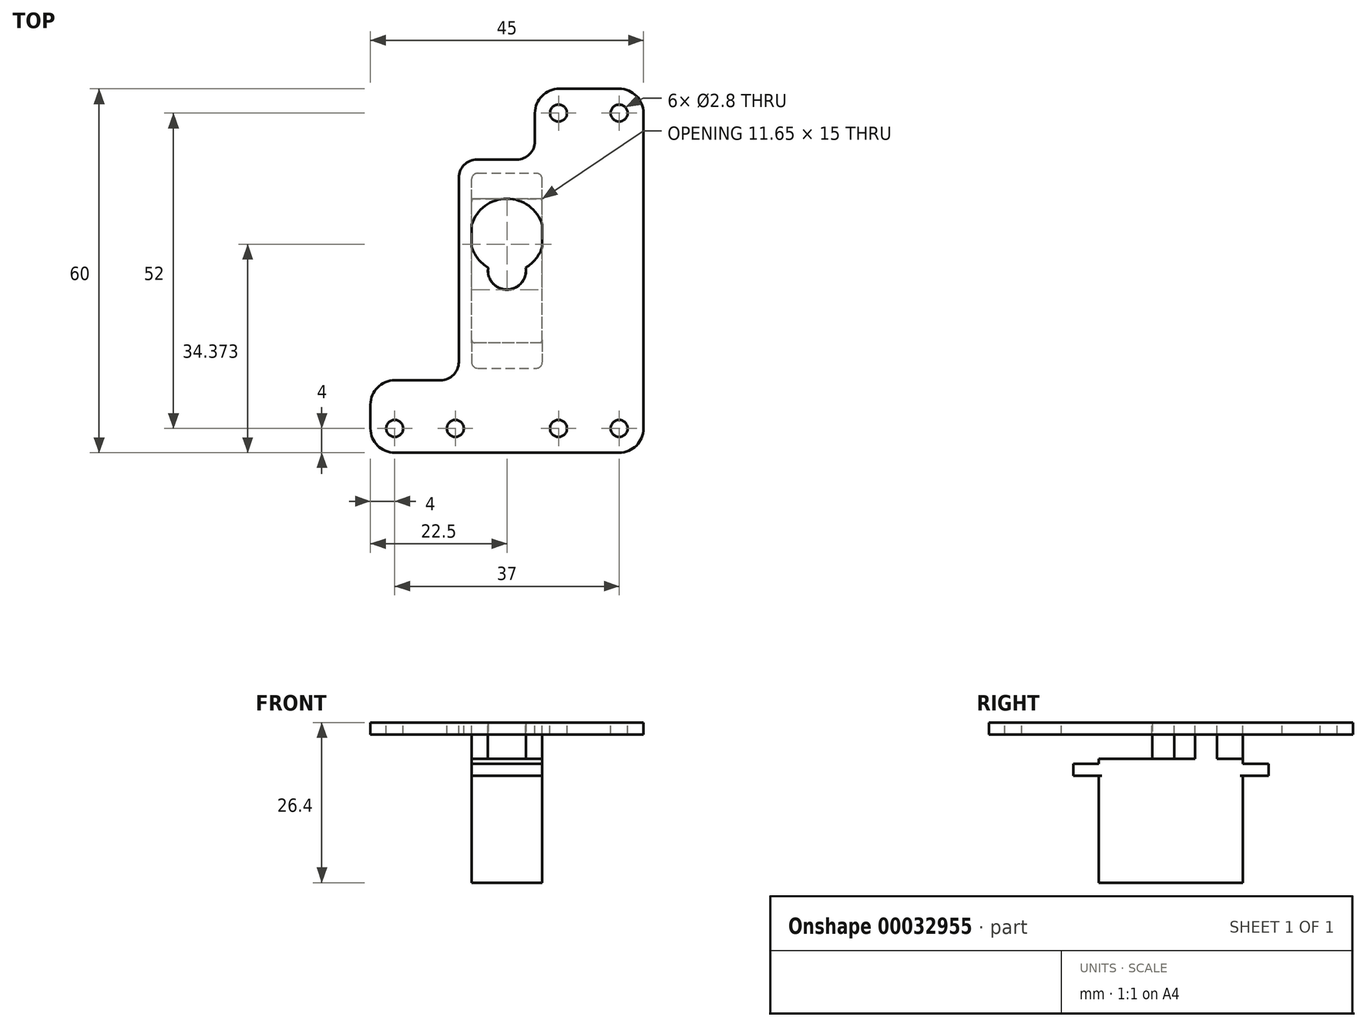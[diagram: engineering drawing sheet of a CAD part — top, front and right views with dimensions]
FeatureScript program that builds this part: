
annotation { "Feature Type Name" : "Feature", "Feature Type Description" : "" }
export const myFeature = defineFeature(function(context is Context, id is Id, definition is map)
    precondition{}
    {
        {
            var Q0;
            Q0=qCreatedBy(makeId("Top.planeOp"),FACE);
            var sketch = newSketch(context, id + "F0", { "sketchPlane" : qUnion([Q0])});
            skLineSegment(sketch, "E0.rect.bottom", {"start": v(5.82, -11.88) * mm, "end": v(-5.83, -11.88) * mm});
            skLineSegment(sketch, "E0.rect.top", {"start": v(5.83, 11.88) * mm, "end": v(-5.82, 11.88) * mm});
            skLineSegment(sketch, "E0.rect.left", {"start": v(5.82, -11.88) * mm, "end": v(5.83, 11.88) * mm});
            skLineSegment(sketch, "E0.rect.right", {"start": v(-5.83, -11.88) * mm, "end": v(-5.82, 11.87) * mm});
            skPoint(sketch, "E0.rect.middle", {"position": v(0, 0) * mm});
            skSolve(sketch);
        }
        {
            var Q0;
            Q0 = qSketchRegion(id + "F0", true);
            extrude(context, id + "F1", {"entities" : qUnion([Q0]), "depth" : 20.4 * mm});
        }
        {
            var Q0;
            Q0=makeQuery(id+"F1.opExtrude","CAP_FACE",FACE,{"disambiguationData":[OSD([sQuery(id+"F0.wireOp",EDGE,"E0.rect.bottom"),sQuery(id+"F0.wireOp",EDGE,"E0.rect.top"),sQuery(id+"F0.wireOp",EDGE,"E0.rect.left"),sQuery(id+"F0.wireOp",EDGE,"E0.rect.right")])],"isStart":false});
            var sketch = newSketch(context, id + "F2", { "sketchPlane" : qUnion([Q0])});
            skArc(sketch, "E1", {"start": v(5.83, 7.59) * mm, "mid": v(0, 11.88) * mm, "end": v(-5.83, 7.59) * mm});
            skLineSegment(sketch, "E2", {"start": v(5.83, 7.59) * mm, "end": v(5.83, 3.96) * mm});
            skLineSegment(sketch, "E3.MirrorCS", {"start": v(-5.83, 7.59) * mm, "end": v(-5.83, 3.96) * mm});
            skArc(sketch, "E4.trimOffspring", {"start": v(-5.83, 3.96) * mm, "mid": v(-4.78, 1.98) * mm, "end": v(-3.09, 0.51) * mm});
            skArc(sketch, "E5", {"start": v(-3.09, 0.51) * mm, "mid": v(0, -3.1) * mm, "end": v(3.09, 0.51) * mm});
            skArc(sketch, "E6.trimOffspring", {"start": v(3.09, 0.51) * mm, "mid": v(4.78, 1.98) * mm, "end": v(5.83, 3.96) * mm});
            skSolve(sketch);
        }
        {
            var Q0;
            Q0 = qSketchRegion(id + "F2", true);
            extrude(context, id + "F3", {"entities" : qUnion([Q0]), "operationType" : NewBodyOperationType.ADD, "depth" : 6 * mm});
        }
        {
            var Q0;
            {var subQ0=sQuery(id+"F0.wireOp",EDGE,"E0.rect.bottom");var subQ1=sQuery(id+"F0.wireOp",EDGE,"E0.rect.left");var subQ2=sQuery(id+"F0.wireOp",EDGE,"E0.rect.right");Q0=makeQuery(id+"F3.boolean.opBoolean","SPLIT",FACE,{"disambiguationData":[TD([makeQuery(id+"F1.opExtrude","SWEPT_FACE",FACE,{"disambiguationData":[OSD([subQ0])]}),makeQuery(id+"F1.opExtrude","SWEPT_FACE",FACE,{"disambiguationData":[OSD([subQ1])]}),makeQuery(id+"F1.opExtrude","SWEPT_FACE",FACE,{"disambiguationData":[OSD([subQ2])]}),makeQuery(id+"F3.opExtrude","SWEPT_FACE",FACE,{"disambiguationData":[OSD([sQuery(id+"F2.wireOp",EDGE,"E2")])]}),makeQuery(id+"F3.opExtrude","SWEPT_FACE",FACE,{"disambiguationData":[OSD([sQuery(id+"F2.wireOp",EDGE,"E3.MirrorCS")])]}),makeQuery(id+"F3.opExtrude","SWEPT_FACE",FACE,{"disambiguationData":[OSD([sQuery(id+"F2.wireOp",EDGE,"E4.trimOffspring")])]}),makeQuery(id+"F3.opExtrude","SWEPT_FACE",FACE,{"disambiguationData":[OSD([sQuery(id+"F2.wireOp",EDGE,"E5")])]}),makeQuery(id+"F3.opExtrude","SWEPT_FACE",FACE,{"disambiguationData":[OSD([sQuery(id+"F2.wireOp",EDGE,"E6.trimOffspring")])]})])],"derivedFrom":makeQuery(id+"F1.opExtrude","CAP_FACE",FACE,{"disambiguationData":[OSD([subQ0,sQuery(id+"F0.wireOp",EDGE,"E0.rect.top"),subQ1,subQ2])],"isStart":false})});}
            var sketch = newSketch(context, id + "F4", { "sketchPlane" : qUnion([Q0])});
            skLineSegment(sketch, "E7.bottom", {"start": v(-5.83, -11.88) * mm, "end": v(5.82, -11.88) * mm});
            skLineSegment(sketch, "E7.top", {"start": v(-5.83, -16.08) * mm, "end": v(5.82, -16.08) * mm});
            skLineSegment(sketch, "E7.left", {"start": v(-5.83, -11.88) * mm, "end": v(-5.83, -16.08) * mm});
            skLineSegment(sketch, "E7.right", {"start": v(5.82, -11.88) * mm, "end": v(5.82, -16.08) * mm});
            skLineSegment(sketch, "E8.MirrorCS", {"start": v(-5.83, 11.88) * mm, "end": v(-5.83, 16.08) * mm});
            skLineSegment(sketch, "E9.MirrorCS", {"start": v(-5.83, 16.08) * mm, "end": v(5.82, 16.08) * mm});
            skLineSegment(sketch, "E10.MirrorCS", {"start": v(5.82, 11.88) * mm, "end": v(5.82, 16.08) * mm});
            skLineSegment(sketch, "E11.MirrorCS", {"start": v(-5.83, 11.88) * mm, "end": v(5.82, 11.88) * mm});
            skSolve(sketch);
        }
        {
            var Q0;
            Q0=makeQuery(id+"F4.imprint","IMPRINT",FACE,{"disambiguationData":[TD([[makeQuery(id+"F4.imprint","IMPRINT",EDGE,{"derivedFrom":sQuery(id+"F4.wireOp",EDGE,"E7.bottom")}),1.0]])]});
            var Q1;
            Q1=makeQuery(id+"F4.imprint","IMPRINT",FACE,{"disambiguationData":[TD([[makeQuery(id+"F4.imprint","IMPRINT",EDGE,{"derivedFrom":sQuery(id+"F4.wireOp",EDGE,"E8.MirrorCS")}),-1.0]])]});
            extrude(context, id + "F5", {"entities" : qUnion([Q0, Q1]), "operationType" : NewBodyOperationType.ADD, "oppositeDirection" : true, "depth" : 2.8 * mm, "hasSecondDirection" : true, "secondDirectionOppositeDirection" : true, "secondDirectionDepth" : .8 * mm});
        }
        {
            var Q0;
            {var subQ0=sQuery(id+"F0.wireOp",EDGE,"E0.rect.top");var subQ1=sQuery(id+"F0.wireOp",EDGE,"E0.rect.left");Q0=makeQuery(id+"F5.boolean.opBoolean","SPLIT",EDGE,{"disambiguationData":[TD([makeQuery(id+"F1.opExtrude","CAP_FACE",FACE,{"disambiguationData":[OSD([sQuery(id+"F0.wireOp",EDGE,"E0.rect.bottom"),subQ0,subQ1,sQuery(id+"F0.wireOp",EDGE,"E0.rect.right")])],"isStart":true})])],"derivedFrom":makeQuery(id+"F1.opExtrude","SWEPT_EDGE",EDGE,{"disambiguationData":[OSD([subQ0,subQ1])]})});}
            var Q1;
            {var subQ0=sQuery(id+"F0.wireOp",EDGE,"E0.rect.bottom");var subQ1=sQuery(id+"F0.wireOp",EDGE,"E0.rect.left");Q1=makeQuery(id+"F5.boolean.opBoolean","SPLIT",EDGE,{"disambiguationData":[TD([makeQuery(id+"F1.opExtrude","CAP_FACE",FACE,{"disambiguationData":[OSD([subQ0,sQuery(id+"F0.wireOp",EDGE,"E0.rect.top"),subQ1,sQuery(id+"F0.wireOp",EDGE,"E0.rect.right")])],"isStart":true})])],"derivedFrom":makeQuery(id+"F1.opExtrude","SWEPT_EDGE",EDGE,{"disambiguationData":[OSD([subQ0,subQ1])]})});}
            var Q2;
            {var subQ0=sQuery(id+"F0.wireOp",EDGE,"E0.rect.bottom");var subQ1=sQuery(id+"F0.wireOp",EDGE,"E0.rect.right");Q2=makeQuery(id+"F5.boolean.opBoolean","SPLIT",EDGE,{"disambiguationData":[TD([makeQuery(id+"F1.opExtrude","CAP_FACE",FACE,{"disambiguationData":[OSD([subQ0,sQuery(id+"F0.wireOp",EDGE,"E0.rect.top"),sQuery(id+"F0.wireOp",EDGE,"E0.rect.left"),subQ1])],"isStart":true})])],"derivedFrom":makeQuery(id+"F1.opExtrude","SWEPT_EDGE",EDGE,{"disambiguationData":[OSD([subQ0,subQ1])]})});}
            var Q3;
            {var subQ0=sQuery(id+"F0.wireOp",EDGE,"E0.rect.top");var subQ1=sQuery(id+"F0.wireOp",EDGE,"E0.rect.right");Q3=makeQuery(id+"F5.boolean.opBoolean","SPLIT",EDGE,{"disambiguationData":[TD([makeQuery(id+"F1.opExtrude","CAP_FACE",FACE,{"disambiguationData":[OSD([sQuery(id+"F0.wireOp",EDGE,"E0.rect.bottom"),subQ0,sQuery(id+"F0.wireOp",EDGE,"E0.rect.left"),subQ1])],"isStart":true})])],"derivedFrom":makeQuery(id+"F1.opExtrude","SWEPT_EDGE",EDGE,{"disambiguationData":[OSD([subQ0,subQ1])]})});}
            fillet(context, id + "F6", {"entities" : qUnion([Q0, Q1, Q2, Q3]), "radius" : .5 * mm, "tangentPropagation" : true, "allowEdgeOverflow" : false});
        }
        {
            var Q0;
            Q0=makeQuery(id+"F5.opExtrude","SWEPT_EDGE",EDGE,{"disambiguationData":[OSD([sQuery(id+"F4.wireOp",EDGE,"E8.MirrorCS"),sQuery(id+"F4.wireOp",EDGE,"E9.MirrorCS")])]});
            var Q1;
            Q1=makeQuery(id+"F5.opExtrude","SWEPT_EDGE",EDGE,{"disambiguationData":[OSD([sQuery(id+"F4.wireOp",EDGE,"E9.MirrorCS"),sQuery(id+"F4.wireOp",EDGE,"E10.MirrorCS")])]});
            var Q2;
            Q2=makeQuery(id+"F5.opExtrude","SWEPT_EDGE",EDGE,{"disambiguationData":[OSD([sQuery(id+"F4.wireOp",EDGE,"E7.top"),sQuery(id+"F4.wireOp",EDGE,"E7.right")])]});
            var Q3;
            Q3=makeQuery(id+"F5.opExtrude","SWEPT_EDGE",EDGE,{"disambiguationData":[OSD([sQuery(id+"F4.wireOp",EDGE,"E7.top"),sQuery(id+"F4.wireOp",EDGE,"E7.left")])]});
            fillet(context, id + "F7", {"entities" : qUnion([Q0, Q1, Q2, Q3]), "radius" : 1 * mm, "tangentPropagation" : true, "allowEdgeOverflow" : false});
        }
        {
            var Q0;
            Q0=makeQuery(id+"F3.opExtrude","CAP_FACE",FACE,{"disambiguationData":[OSD([sQuery(id+"F2.wireOp",EDGE,"E1"),sQuery(id+"F2.wireOp",EDGE,"E2"),sQuery(id+"F2.wireOp",EDGE,"E3.MirrorCS"),sQuery(id+"F2.wireOp",EDGE,"E4.trimOffspring"),sQuery(id+"F2.wireOp",EDGE,"E5"),sQuery(id+"F2.wireOp",EDGE,"E6.trimOffspring")])],"isStart":false});
            var sketch = newSketch(context, id + "F8", { "sketchPlane" : qUnion([Q0])});
            skArc(sketch, "E12", {"start": v(3.09, 0.51) * mm, "mid": v(4.78, 1.98) * mm, "end": v(5.83, 3.96) * mm});
            skArc(sketch, "E13", {"start": v(-3.09, 0.51) * mm, "mid": v(0, -3.13) * mm, "end": v(3.09, 0.51) * mm});
            skLineSegment(sketch, "E14", {"start": v(-5.83, 3.96) * mm, "end": v(-5.83, 7.59) * mm});
            skLineSegment(sketch, "E15.MirrorCS", {"start": v(5.83, 3.96) * mm, "end": v(5.83, 7.59) * mm});
            skArc(sketch, "E16.trimOffspring", {"start": v(-5.83, 3.96) * mm, "mid": v(-4.78, 1.98) * mm, "end": v(-3.09, 0.51) * mm});
            skArc(sketch, "E17.trimOffspring", {"start": v(5.83, 7.59) * mm, "mid": v(0, 11.88) * mm, "end": v(-5.83, 7.59) * mm});
            skLineSegment(sketch, "E18.rect.bottom", {"start": v(22.5, 30) * mm, "end": v(4.61, 30) * mm});
            skLineSegment(sketch, "E18.rect.top", {"start": v(22.5, -30) * mm, "end": v(-22.5, -30) * mm});
            skLineSegment(sketch, "E18.rect.left", {"start": v(22.5, 30) * mm, "end": v(22.5, -30) * mm});
            skLineSegment(sketch, "E18.rect.right", {"start": v(-22.5, -18.07) * mm, "end": v(-22.5, -30) * mm});
            skLineSegment(sketch, "E19.bottom", {"start": v(-22.5, -30) * mm, "end": v(-18.5, -30) * mm, "construction": true});
            skLineSegment(sketch, "E19.top", {"start": v(-22.5, -26) * mm, "end": v(-18.5, -26) * mm, "construction": true});
            skLineSegment(sketch, "E19.left", {"start": v(-22.5, -30) * mm, "end": v(-22.5, -26) * mm, "construction": true});
            skLineSegment(sketch, "E19.right", {"start": v(-18.5, -30) * mm, "end": v(-18.5, -26) * mm, "construction": true});
            skCircle(sketch, "E20", {"center": v(-18.5, -26) * mm, "radius": 1.4 * mm});
            skCircle(sketch, "E21.MirrorC", {"center": v(18.5, -26) * mm, "radius": 1.4 * mm});
            skCircle(sketch, "E22.MirrorC", {"center": v(18.5, 26) * mm, "radius": 1.4 * mm});
            skCircle(sketch, "E23", {"center": v(-8.5, -26) * mm, "radius": 1.4 * mm});
            skCircle(sketch, "E24.MirrorC", {"center": v(8.5, -26) * mm, "radius": 1.4 * mm});
            skCircle(sketch, "E25.MirrorC", {"center": v(8.5, 26) * mm, "radius": 1.4 * mm});
            skLineSegment(sketch, "E26", {"start": v(4.61, 30) * mm, "end": v(4.61, 21.32) * mm});
            skLineSegment(sketch, "E27", {"start": v(1.61, 18.32) * mm, "end": v(-4.94, 18.32) * mm});
            skLineSegment(sketch, "E28", {"start": v(-7.94, 15.32) * mm, "end": v(-7.94, -15.07) * mm});
            skLineSegment(sketch, "E29", {"start": v(-10.94, -18.07) * mm, "end": v(-22.5, -18.07) * mm});
            skPoint(sketch, "E30.orphan", {"position": v(-22.5, 30) * mm});
            skPoint(sketch, "E31.visualSharp", {"position": v(-7.94, -18.07) * mm});
            skArc(sketch, "E31.filletArc", {"start": v(-10.94, -18.07) * mm, "mid": v(-8.82, -17.19) * mm, "end": v(-7.94, -15.07) * mm});
            skPoint(sketch, "E32.visualSharp", {"position": v(4.61, 18.32) * mm});
            skArc(sketch, "E32.filletArc", {"start": v(1.61, 18.32) * mm, "mid": v(3.73, 19.2) * mm, "end": v(4.61, 21.32) * mm});
            skPoint(sketch, "E33.visualSharp", {"position": v(-7.94, 18.32) * mm});
            skArc(sketch, "E33.filletArc", {"start": v(-4.94, 18.32) * mm, "mid": v(-7.07, 17.44) * mm, "end": v(-7.94, 15.32) * mm});
            skSolve(sketch);
        }
        {
            var Q0;
            Q0 = qSketchRegion(id + "F8", true);
            extrude(context, id + "F9", {"entities" : qUnion([Q0]), "oppositeDirection" : true, "depth" : 2 * mm});
        }
        {
            var Q0;
            Q0=makeQuery(id+"F9.opExtrude","SWEPT_EDGE",EDGE,{"disambiguationData":[OSD([sQuery(id+"F8.wireOp",EDGE,"E18.rect.top"),sQuery(id+"F8.wireOp",EDGE,"E18.rect.right")])]});
            var Q1;
            Q1=makeQuery(id+"F9.opExtrude","SWEPT_EDGE",EDGE,{"disambiguationData":[OSD([sQuery(id+"F8.wireOp",EDGE,"E18.rect.bottom"),sQuery(id+"F8.wireOp",EDGE,"E18.rect.right")])]});
            var Q2;
            Q2=makeQuery(id+"F9.opExtrude","SWEPT_EDGE",EDGE,{"disambiguationData":[OSD([sQuery(id+"F8.wireOp",EDGE,"E18.rect.bottom"),sQuery(id+"F8.wireOp",EDGE,"E18.rect.left")])]});
            var Q3;
            Q3=makeQuery(id+"F9.opExtrude","SWEPT_EDGE",EDGE,{"disambiguationData":[OSD([sQuery(id+"F8.wireOp",EDGE,"E18.rect.top"),sQuery(id+"F8.wireOp",EDGE,"E18.rect.left")])]});
            fillet(context, id + "F10", {"entities" : qUnion([Q0, Q1, Q2, Q3]), "radius" : 4 * mm, "tangentPropagation" : true, "allowEdgeOverflow" : false});
        }
        {
            var Q0;
            Q0=makeQuery(id+"F9.opExtrude","SWEPT_BODY",BODY,{"disambiguationData":[OSD([sQuery(id+"F8.wireOp",EDGE,"E12"),sQuery(id+"F8.wireOp",EDGE,"E13"),sQuery(id+"F8.wireOp",EDGE,"E14"),sQuery(id+"F8.wireOp",EDGE,"E15.MirrorCS"),sQuery(id+"F8.wireOp",EDGE,"E16.trimOffspring"),sQuery(id+"F8.wireOp",EDGE,"E17.trimOffspring"),sQuery(id+"F8.wireOp",EDGE,"E18.rect.bottom"),sQuery(id+"F8.wireOp",EDGE,"E18.rect.top"),sQuery(id+"F8.wireOp",EDGE,"E18.rect.left"),sQuery(id+"F8.wireOp",EDGE,"E18.rect.right"),sQuery(id+"F8.wireOp",EDGE,"E20"),sQuery(id+"F8.wireOp",EDGE,"ce85554a-ae08-408d-bbdd-004999f886530.MirrorC"),sQuery(id+"F8.wireOp",EDGE,"E21.MirrorC"),sQuery(id+"F8.wireOp",EDGE,"E22.MirrorC"),sQuery(id+"F8.wireOp",EDGE,"E23"),sQuery(id+"F8.wireOp",EDGE,"E24.MirrorC"),sQuery(id+"F8.wireOp",EDGE,"46118b25-6d7d-4224-8583-2d73bb83e9220.MirrorC"),sQuery(id+"F8.wireOp",EDGE,"E25.MirrorC")])]});
            transform(context, id + "F11", {"entities" : qUnion([Q0]), "transformType" : TransformType.TRANSLATION_3D, "dx" : 0 * mm, "dy" : 0 * mm, "dz" : 0 * mm, "makeCopy" : true});
        }
        {
            var Q0;
            Q0=makeQuery(id+"F11.opPattern","COPY",BODY,{"derivedFrom":makeQuery(id+"F9.opExtrude","SWEPT_BODY",BODY,{"disambiguationData":[OSD([sQuery(id+"F8.wireOp",EDGE,"E12"),sQuery(id+"F8.wireOp",EDGE,"E13"),sQuery(id+"F8.wireOp",EDGE,"E14"),sQuery(id+"F8.wireOp",EDGE,"E15.MirrorCS"),sQuery(id+"F8.wireOp",EDGE,"E16.trimOffspring"),sQuery(id+"F8.wireOp",EDGE,"E17.trimOffspring"),sQuery(id+"F8.wireOp",EDGE,"E18.rect.bottom"),sQuery(id+"F8.wireOp",EDGE,"E18.rect.top"),sQuery(id+"F8.wireOp",EDGE,"E18.rect.left"),sQuery(id+"F8.wireOp",EDGE,"E18.rect.right"),sQuery(id+"F8.wireOp",EDGE,"E20"),sQuery(id+"F8.wireOp",EDGE,"E21.MirrorC"),sQuery(id+"F8.wireOp",EDGE,"E22.MirrorC"),sQuery(id+"F8.wireOp",EDGE,"E23"),sQuery(id+"F8.wireOp",EDGE,"E24.MirrorC"),sQuery(id+"F8.wireOp",EDGE,"E25.MirrorC"),sQuery(id+"F8.wireOp",EDGE,"E26"),sQuery(id+"F8.wireOp",EDGE,"E27"),sQuery(id+"F8.wireOp",EDGE,"E28"),sQuery(id+"F8.wireOp",EDGE,"E29"),sQuery(id+"F8.wireOp",EDGE,"E31.filletArc"),sQuery(id+"F8.wireOp",EDGE,"E32.filletArc"),sQuery(id+"F8.wireOp",EDGE,"E33.filletArc")])]}),"instanceName":"1"});
            deleteBodies(context, id + "F12", {"entities" : qUnion([Q0])});
        }
    });
